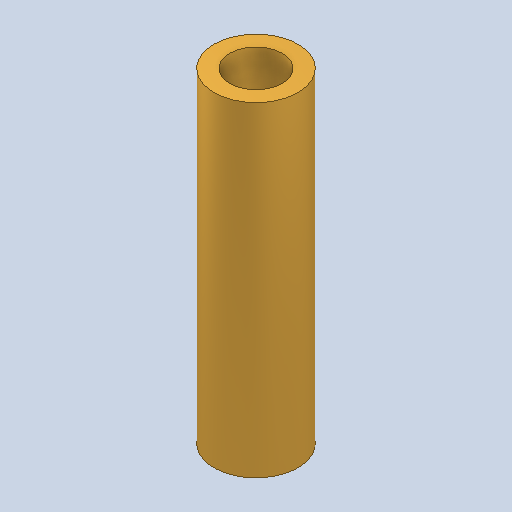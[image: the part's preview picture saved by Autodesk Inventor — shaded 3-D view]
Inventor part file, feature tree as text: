
AUTODESK INVENTOR PART (.ipt)
format: ipt  version: 2023 (Build 270158000, 158)  size: 247,296 bytes
history: native  units: mm
features: other x1, extrude x1, hole x1, sketch x1
ambient origin geometry x8: Origin, YZ Plane, XZ Plane, XY Plane, X Axis, Y Axis, Z Axis, Center Point
bodies: Body1 (feature_tree)
feature tree (4):
  other  "Sólido1"
  extrude  "Extrusão1"  Depth=31.0mm TaperAngle=0.0deg
  hole  "Furo1"  [1 undecoded]
  sketch  "Esboço2"  dims[d1=8.0mm d2=31.0mm d3=0.0mm d4=5.0mm d5=10.0mm d6=4.0mm d7=2.0mm d8=90.0deg d9=0.5mm d10=20.594885mm]
note: 1 required parameter value undecoded (feature->parameter linkage not recoverable at this tier; creation-order binding heuristic only, values carry confidence <= 0.55)
